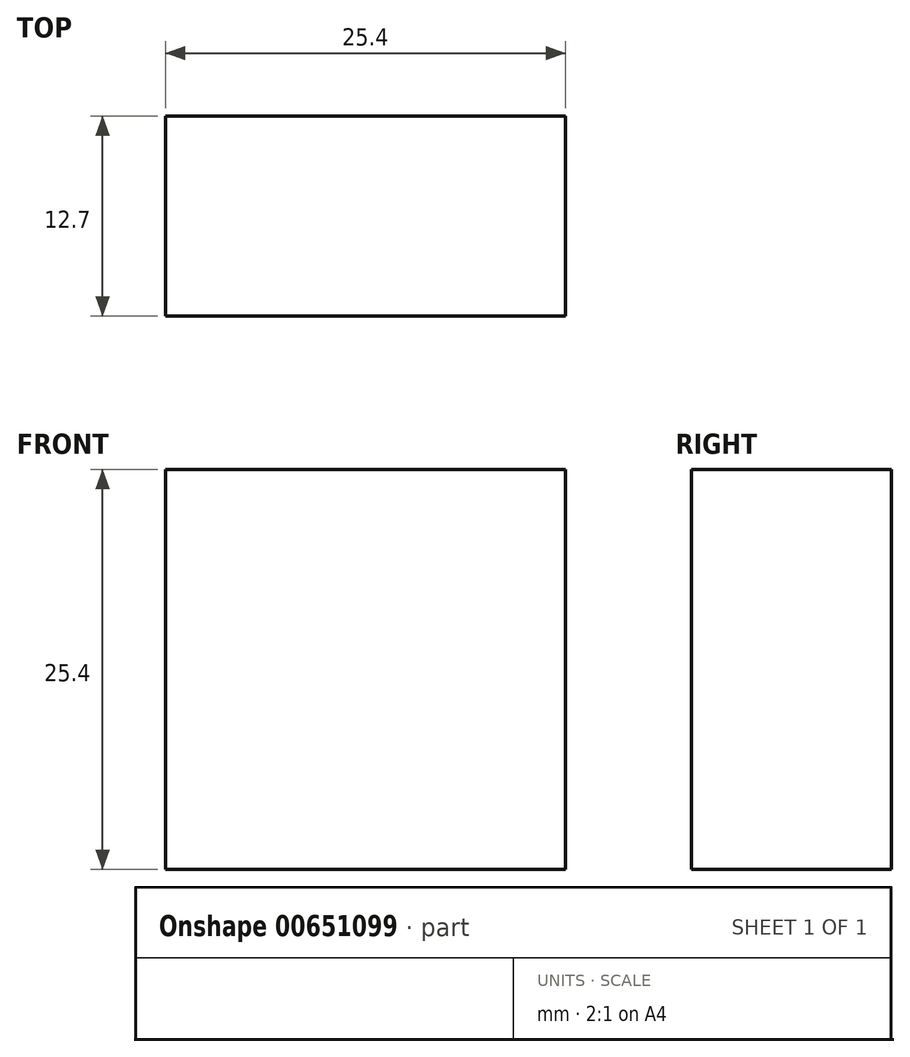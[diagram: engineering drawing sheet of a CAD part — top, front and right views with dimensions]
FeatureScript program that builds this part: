
annotation { "Feature Type Name" : "Feature", "Feature Type Description" : "" }
export const myFeature = defineFeature(function(context is Context, id is Id, definition is map)
    precondition{}
    {
        {
            var Q0;
            Q0=qCreatedBy(makeId("Front.planeOp"),FACE);
            var sketch = newSketch(context, id + "F0", { "sketchPlane" : qUnion([Q0])});
            skLineSegment(sketch, "E0.bottom", {"start": v(-12.7, 12.7) * mm, "end": v(12.7, 12.7) * mm});
            skLineSegment(sketch, "E0.top", {"start": v(-12.7, -12.7) * mm, "end": v(12.7, -12.7) * mm});
            skLineSegment(sketch, "E0.left", {"start": v(-12.7, 12.7) * mm, "end": v(-12.7, -12.7) * mm});
            skLineSegment(sketch, "E0.right", {"start": v(12.7, 12.7) * mm, "end": v(12.7, -12.7) * mm});
            skPoint(sketch, "E0.middle", {"position": v(0, 0) * mm});
            skSolve(sketch);
        }
        {
            var Q0;
            Q0 = qSketchRegion(id + "F0", true);
            extrude(context, id + "F1", {"entities" : qUnion([Q0]), "depth" : 12.7 * mm, "offsetDistance" : 25.4 * mm});
        }
    });
